# Revit family: Zumtobel basicDIM ILD G2 SFI 20 16DPI
name_source: partatom
category: Lighting Devices
units: mm (PartAtom-declared; Revit-internal decimal feet)

## family parameters
Cut with Voids When Loaded = Yes
Host = Face
Maintain Annotation Orientation = No
OmniClass Number = 23.85.80.11.27
OmniClass Title = Lighting Controls
Part Type = Normal
Room Calculation Point = Yes
Round Connector Dimension = Use Diameter
Shared = No

## types (2) — shared parameters
Assembly Code = D5030800
Description = Motion Sensor
Manufacturer = Zumtobel Lighting
Material-Housing = ZG-Lighting Fixtures-Plastic-White_RGB 255 255 255
Type Image = basicDIM ILD G2 SFI 20 16DPI WH.jpg
URL = https://www.zumtobel.com
zero-valued in all types: Default Elevation

## per-type parameters (varying)
| type | Model | Offset | Sensor housing ACU 033 IP65 WH |
| basicDIM ILD G2 SFI 20 16DPI WH | 28003393 | 0 mm  [stored 0 ft] | No |
| basicDIM ILD G2 SFI 20 16DPI WH + Sensor housing ACU 033 IP65 WH | 28003393 + 28003393 | 65 mm  [stored 0.213255 ft] | Yes |

note: [stored X ft] marks values corroborated as IEEE doubles in the binary element streams (Revit-internal decimal feet)

## geometry (parser evidence)
native form markers: Sweep x2
no freeform markers — native parametric forms only
